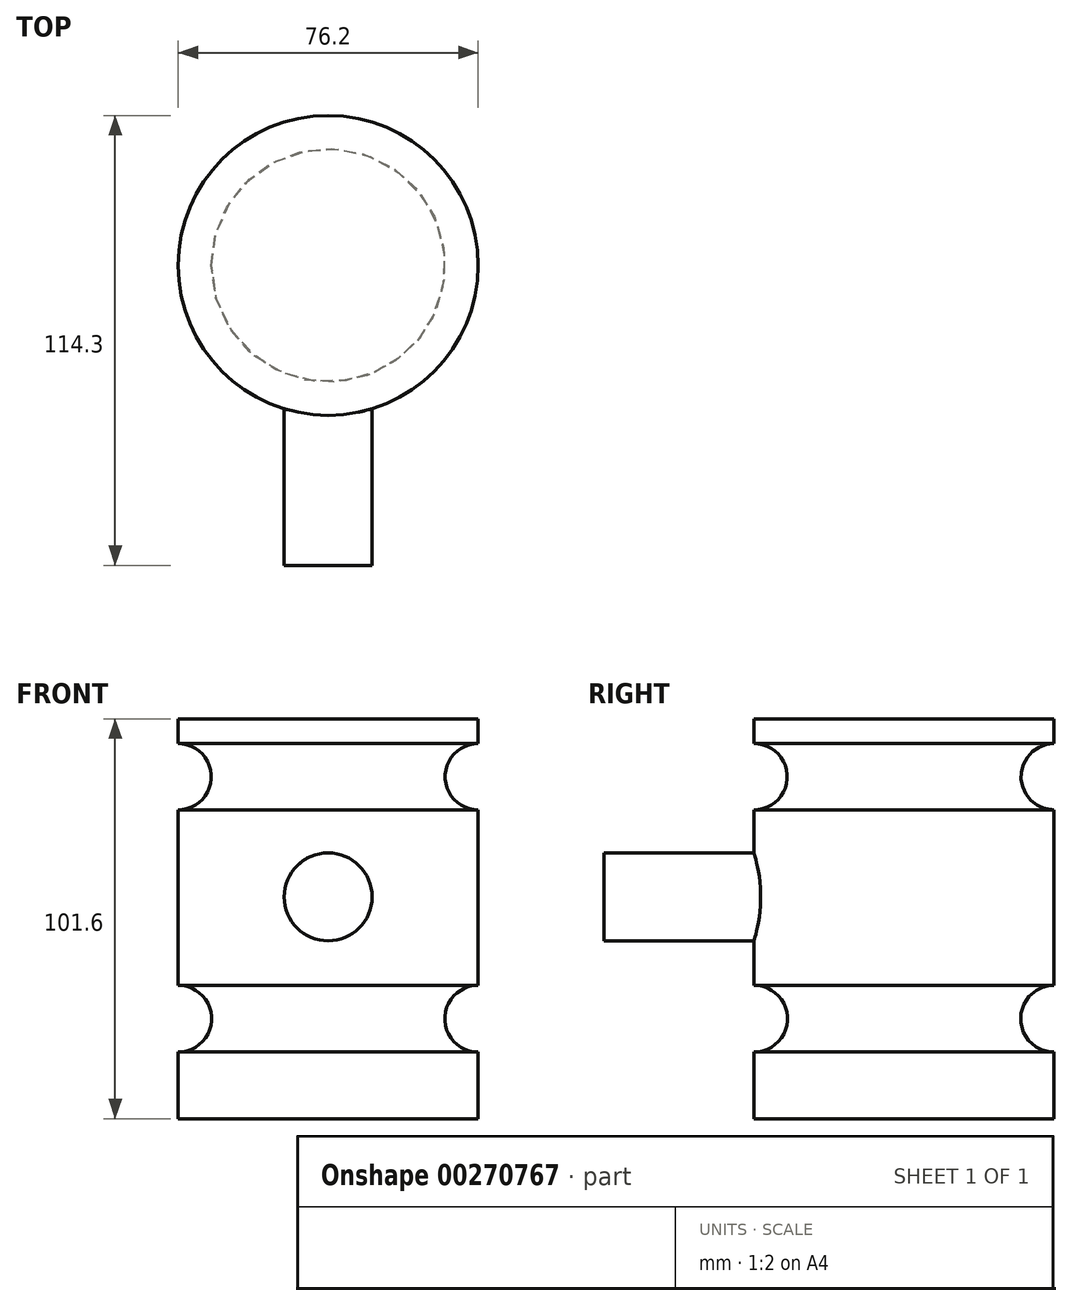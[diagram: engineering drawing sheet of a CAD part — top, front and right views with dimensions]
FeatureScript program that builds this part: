
annotation { "Feature Type Name" : "Feature", "Feature Type Description" : "" }
export const myFeature = defineFeature(function(context is Context, id is Id, definition is map)
    precondition{}
    {
        {
            var Q0;
            Q0=qCreatedBy(makeId("Front.planeOp"),FACE);
            var sketch = newSketch(context, id + "F0", { "sketchPlane" : qUnion([Q0])});
            skLineSegment(sketch, "E0.bottom", {"start": v(0, 0) * mm, "end": v(-38.1, 0) * mm});
            skLineSegment(sketch, "E0.top", {"start": v(0, 101.6) * mm, "end": v(-38.1, 101.6) * mm});
            skLineSegment(sketch, "E0.left", {"start": v(0, 0) * mm, "end": v(0, 101.6) * mm});
            skLineSegment(sketch, "E0.right", {"start": v(-38.1, 0) * mm, "end": v(-38.1, 16.91) * mm});
            skArc(sketch, "E1", {"start": v(-38.1, 78.5) * mm, "mid": v(-29.7, 86.89) * mm, "end": v(-38.1, 95.28) * mm});
            skArc(sketch, "E2", {"start": v(-38.1, 16.91) * mm, "mid": v(-29.61, 25.4) * mm, "end": v(-38.1, 33.89) * mm});
            skLineSegment(sketch, "E3.trimOffspring", {"start": v(-38.1, 33.89) * mm, "end": v(-38.1, 78.5) * mm});
            skLineSegment(sketch, "E4.trimOffspring", {"start": v(-38.1, 95.28) * mm, "end": v(-38.1, 101.6) * mm});
            skSolve(sketch);
        }
        {
            var Q0;
            Q0=makeQuery(id+"F0.imprint","IMPRINT",FACE,{"disambiguationData":[TD([[makeQuery(id+"F0.imprint","IMPRINT",EDGE,{"derivedFrom":sQuery(id+"F0.wireOp",EDGE,"E0.bottom")}),-1.0]])]});
            var Q1;
            Q1=sQuery(id+"F0.wireOp",EDGE,"E0.left");
            revolve(context, id + "F1", {"entities" : qUnion([Q0]), "axis" : qUnion([Q1]), "revolveType" : RevolveType.FULL});
        }
        {
            var Q0;
            Q0=qCreatedBy(makeId("Front.planeOp"),FACE);
            var sketch = newSketch(context, id + "F2", { "sketchPlane" : qUnion([Q0])});
            skCircle(sketch, "E5", {"center": v(0, 56.36) * mm, "radius": 11.17 * mm});
            skSolve(sketch);
        }
        {
            var Q0;
            Q0 = qSketchRegion(id + "F2", true);
            extrude(context, id + "F3", {"entities" : qUnion([Q0]), "operationType" : NewBodyOperationType.ADD, "depth" : 76.2 * mm});
        }
    });
